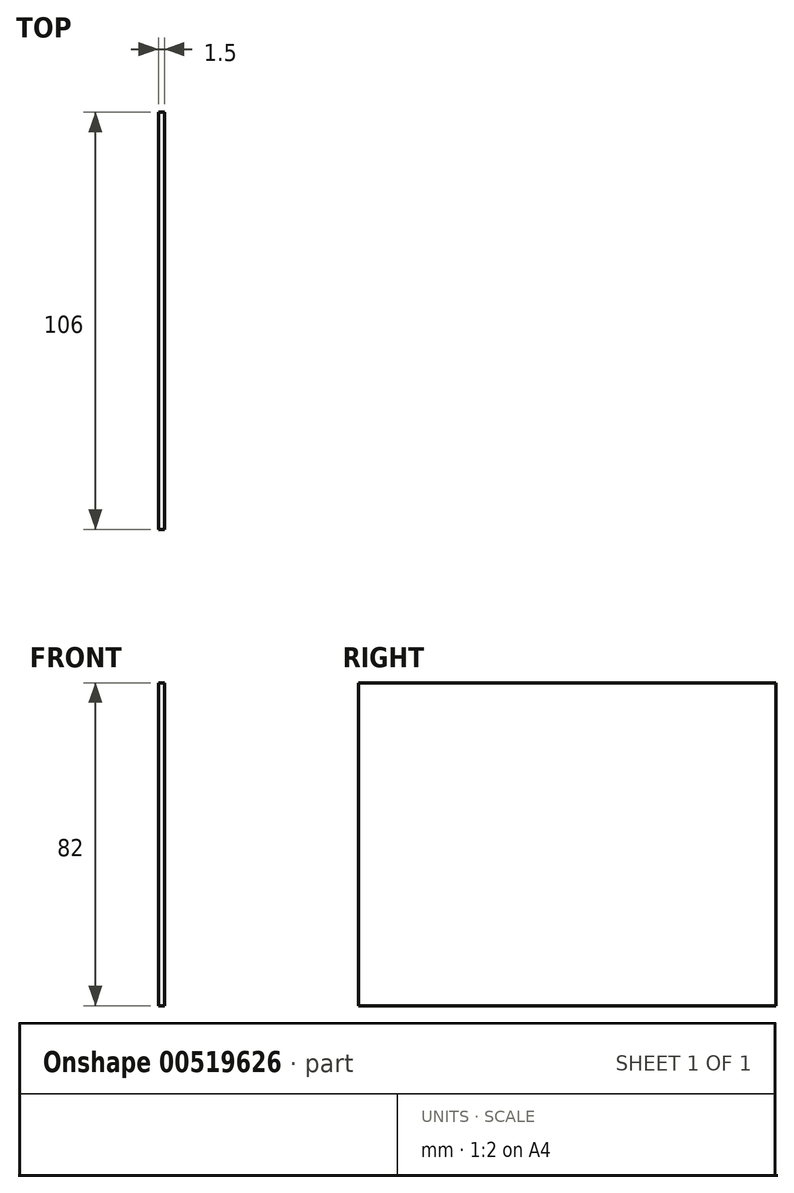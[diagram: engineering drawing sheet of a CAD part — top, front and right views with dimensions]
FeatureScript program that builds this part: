
annotation { "Feature Type Name" : "Feature", "Feature Type Description" : "" }
export const myFeature = defineFeature(function(context is Context, id is Id, definition is map)
    precondition{}
    {
        {
            var Q0;
            Q0=qCreatedBy(makeId("Right.planeOp"),FACE);
            var sketch = newSketch(context, id + "F0", { "sketchPlane" : qUnion([Q0])});
            skLineSegment(sketch, "E0.bottom", {"start": v(53, 41) * mm, "end": v(-53, 41) * mm});
            skLineSegment(sketch, "E0.top", {"start": v(53, -41) * mm, "end": v(-53, -41) * mm});
            skLineSegment(sketch, "E0.left", {"start": v(53, 41) * mm, "end": v(53, -41) * mm});
            skLineSegment(sketch, "E0.right", {"start": v(-53, 41) * mm, "end": v(-53, -41) * mm});
            skPoint(sketch, "E0.middle", {"position": v(0, 0) * mm});
            skSolve(sketch);
        }
        {
            var Q0;
            Q0 = qSketchRegion(id + "F0", true);
            extrude(context, id + "F1", {"entities" : qUnion([Q0]), "depth" : 1.5 * mm, "offsetDistance" : 25 * mm});
        }
    });
